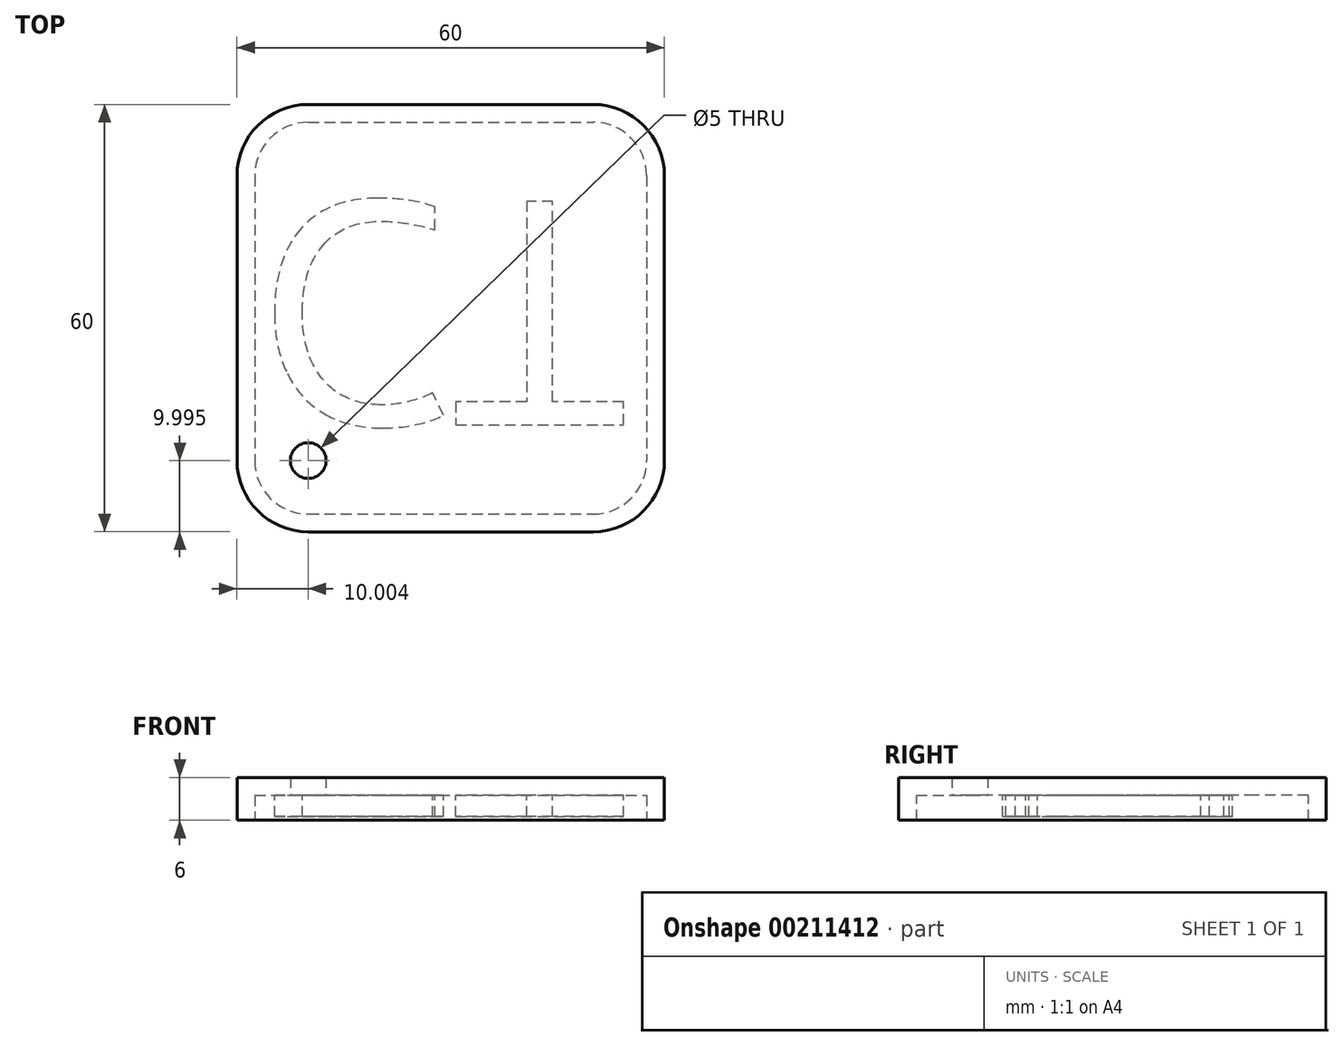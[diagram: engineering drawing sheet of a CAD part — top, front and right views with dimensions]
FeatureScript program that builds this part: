
annotation { "Feature Type Name" : "Feature", "Feature Type Description" : "" }
export const myFeature = defineFeature(function(context is Context, id is Id, definition is map)
    precondition{}
    {
        {
            var Q0;
            Q0=qCreatedBy(makeId("Top.planeOp"),FACE);
            var sketch = newSketch(context, id + "F0", { "sketchPlane" : qUnion([Q0])});
            skLineSegment(sketch, "E0.bottom", {"start": v(-24.5, 28.42) * mm, "end": v(35.5, 28.42) * mm});
            skLineSegment(sketch, "E0.top", {"start": v(-24.5, -31.58) * mm, "end": v(35.5, -31.58) * mm});
            skLineSegment(sketch, "E0.left", {"start": v(-24.5, 28.42) * mm, "end": v(-24.5, -31.58) * mm});
            skLineSegment(sketch, "E0.right", {"start": v(35.5, 28.42) * mm, "end": v(35.5, -31.58) * mm});
            skSolve(sketch);
        }
        {
            var Q0;
            Q0=makeQuery(id+"F0.imprint","IMPRINT",FACE,{"disambiguationData":[TD([[makeQuery(id+"F0.imprint","IMPRINT",EDGE,{"derivedFrom":sQuery(id+"F0.wireOp",EDGE,"E0.bottom")}),-1.0]])]});
            extrude(context, id + "F1", {"entities" : qUnion([Q0]), "depth" : 6 * mm});
        }
        {
            var Q0;
            Q0=makeQuery(id+"F1.opExtrude","SWEPT_EDGE",EDGE,{"disambiguationData":[OSD([sQuery(id+"F0.wireOp",EDGE,"E0.bottom"),sQuery(id+"F0.wireOp",EDGE,"E0.left")])]});
            var Q1;
            Q1=makeQuery(id+"F1.opExtrude","SWEPT_EDGE",EDGE,{"disambiguationData":[OSD([sQuery(id+"F0.wireOp",EDGE,"E0.top"),sQuery(id+"F0.wireOp",EDGE,"E0.left")])]});
            var Q2;
            Q2=makeQuery(id+"F1.opExtrude","SWEPT_EDGE",EDGE,{"disambiguationData":[OSD([sQuery(id+"F0.wireOp",EDGE,"E0.top"),sQuery(id+"F0.wireOp",EDGE,"E0.right")])]});
            var Q3;
            Q3=makeQuery(id+"F1.opExtrude","SWEPT_EDGE",EDGE,{"disambiguationData":[OSD([sQuery(id+"F0.wireOp",EDGE,"E0.bottom"),sQuery(id+"F0.wireOp",EDGE,"E0.right")])]});
            fillet(context, id + "F2", {"entities" : qUnion([Q0, Q1, Q2, Q3]), "radius" : 10 * mm, "tangentPropagation" : true, "allowEdgeOverflow" : false});
        }
        {
            var Q0;
            Q0=makeQuery(id+"F1.opExtrude","CAP_FACE",FACE,{"disambiguationData":[OSD([sQuery(id+"F0.wireOp",EDGE,"E0.bottom"),sQuery(id+"F0.wireOp",EDGE,"E0.top"),sQuery(id+"F0.wireOp",EDGE,"E0.left"),sQuery(id+"F0.wireOp",EDGE,"E0.right")])],"isStart":true});
            shell(context, id + "F3", {"entities" : qUnion([Q0]), "thickness" : 2.5 * mm});
        }
        {
            var Q0;
            Q0=makeQuery(id+"F3.opShell","OFFSET_FACE",FACE,{"disambiguationData":[OSD([sQuery(id+"F0.wireOp",EDGE,"E0.bottom"),sQuery(id+"F0.wireOp",EDGE,"E0.top"),sQuery(id+"F0.wireOp",EDGE,"E0.left"),sQuery(id+"F0.wireOp",EDGE,"E0.right")])]});
            var sketch = newSketch(context, id + "F4", { "sketchPlane" : qUnion([Q0])});
            skText(sketch, "E1", { "text": "CT", "fontName": "OpenSans-Regular.ttf"});
            const initialGuessF4  = {"E1": [-0.02192, -0.01482, 1, 0, 0.03166]};
            skSetInitialGuess(sketch, initialGuessF4);
            skSolve(sketch);
        }
        {
            var Q0;
            Q0 = qSketchRegion(id + "F4", true);
            extrude(context, id + "F5", {"entities" : qUnion([Q0]), "operationType" : NewBodyOperationType.ADD, "depth" : 3 * mm});
        }
        {
            var Q0;
            Q0=makeQuery(id+"F3.opShell","OFFSET_FACE",FACE,{"disambiguationData":[OSD([sQuery(id+"F0.wireOp",EDGE,"E0.bottom"),sQuery(id+"F0.wireOp",EDGE,"E0.top"),sQuery(id+"F0.wireOp",EDGE,"E0.left"),sQuery(id+"F0.wireOp",EDGE,"E0.right")])]});
            var sketch = newSketch(context, id + "F6", { "sketchPlane" : qUnion([Q0])});
            skCircle(sketch, "E2", {"center": v(-14.5, 21.58) * mm, "radius": 3.75 * mm});
            skSolve(sketch);
        }
        {
            var Q0;
            Q0=sQuery(id+"F6.wireOp",VERTEX,"E2.center");
            var Q1;
            Q1=makeQuery(id+"F1.opExtrude","SWEPT_BODY",BODY,{"disambiguationData":[OSD([sQuery(id+"F0.wireOp",EDGE,"E0.bottom"),sQuery(id+"F0.wireOp",EDGE,"E0.top"),sQuery(id+"F0.wireOp",EDGE,"E0.left"),sQuery(id+"F0.wireOp",EDGE,"E0.right")])]});
            hole(context, id + "F7", {"style" : HoleStyle.SIMPLE, "endStyle" : HoleEndStyle.THROUGH, "holeDiameter" : 5 * mm, "locations" : qUnion([Q0]), "scope" : qUnion([Q1]), "isTappedThrough" : true});
        }
    });
